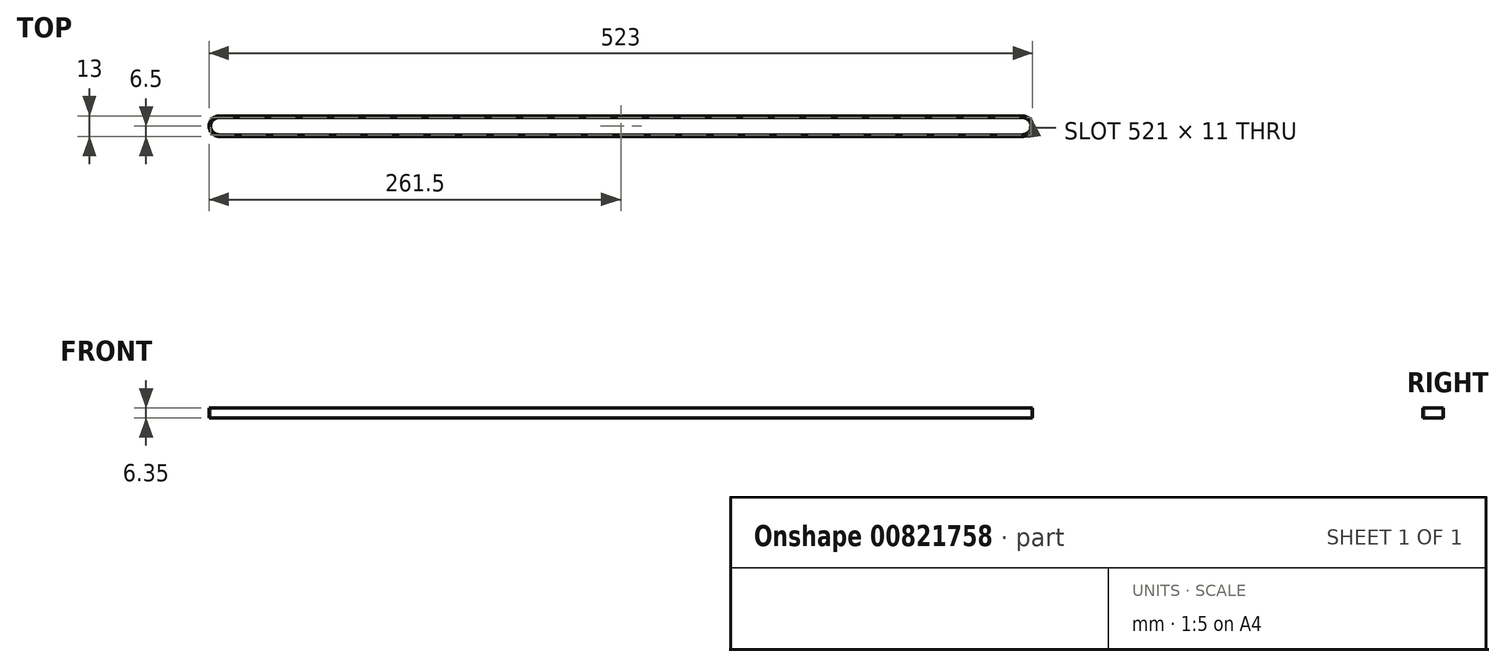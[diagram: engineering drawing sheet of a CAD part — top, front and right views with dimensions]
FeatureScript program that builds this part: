
annotation { "Feature Type Name" : "Feature", "Feature Type Description" : "" }
export const myFeature = defineFeature(function(context is Context, id is Id, definition is map)
    precondition{}
    {
        {
            var Q0;
            Q0=qCreatedBy(makeId("Top.planeOp"),FACE);
            var sketch = newSketch(context, id + "F0", { "sketchPlane" : qUnion([Q0])});
            skLineSegment(sketch, "E0.bottom", {"start": v(-255, 6.5) * mm, "end": v(255, 6.5) * mm});
            skLineSegment(sketch, "E0.top", {"start": v(-255, -6.5) * mm, "end": v(255, -6.5) * mm});
            skPoint(sketch, "E0.middle", {"position": v(0, 0) * mm});
            skArc(sketch, "E1", {"start": v(-255, 6.5) * mm, "mid": v(-261.5, 0) * mm, "end": v(-255, -6.5) * mm});
            skArc(sketch, "E2", {"start": v(255, -6.5) * mm, "mid": v(261.5, 0) * mm, "end": v(255, 6.5) * mm});
            skArc(sketch, "E3.0", {"start": v(255, -5.5) * mm, "mid": v(260.5, 0) * mm, "end": v(255, 5.5) * mm});
            skLineSegment(sketch, "E3.1", {"start": v(-255, -5.5) * mm, "end": v(255, -5.5) * mm});
            skArc(sketch, "E3.2", {"start": v(-255, 5.5) * mm, "mid": v(-260.5, 0) * mm, "end": v(-255, -5.5) * mm});
            skLineSegment(sketch, "E3.3", {"start": v(-255, 5.5) * mm, "end": v(255, 5.5) * mm});
            skSolve(sketch);
        }
        {
            var Q0;
            Q0=qSketchRegion(id+"F0",true);
            extrude(context, id + "F1", {"entities" : qUnion([Q0]), "depth" : 6.35 * mm, "offsetDistance" : 25 * mm});
        }
    });
